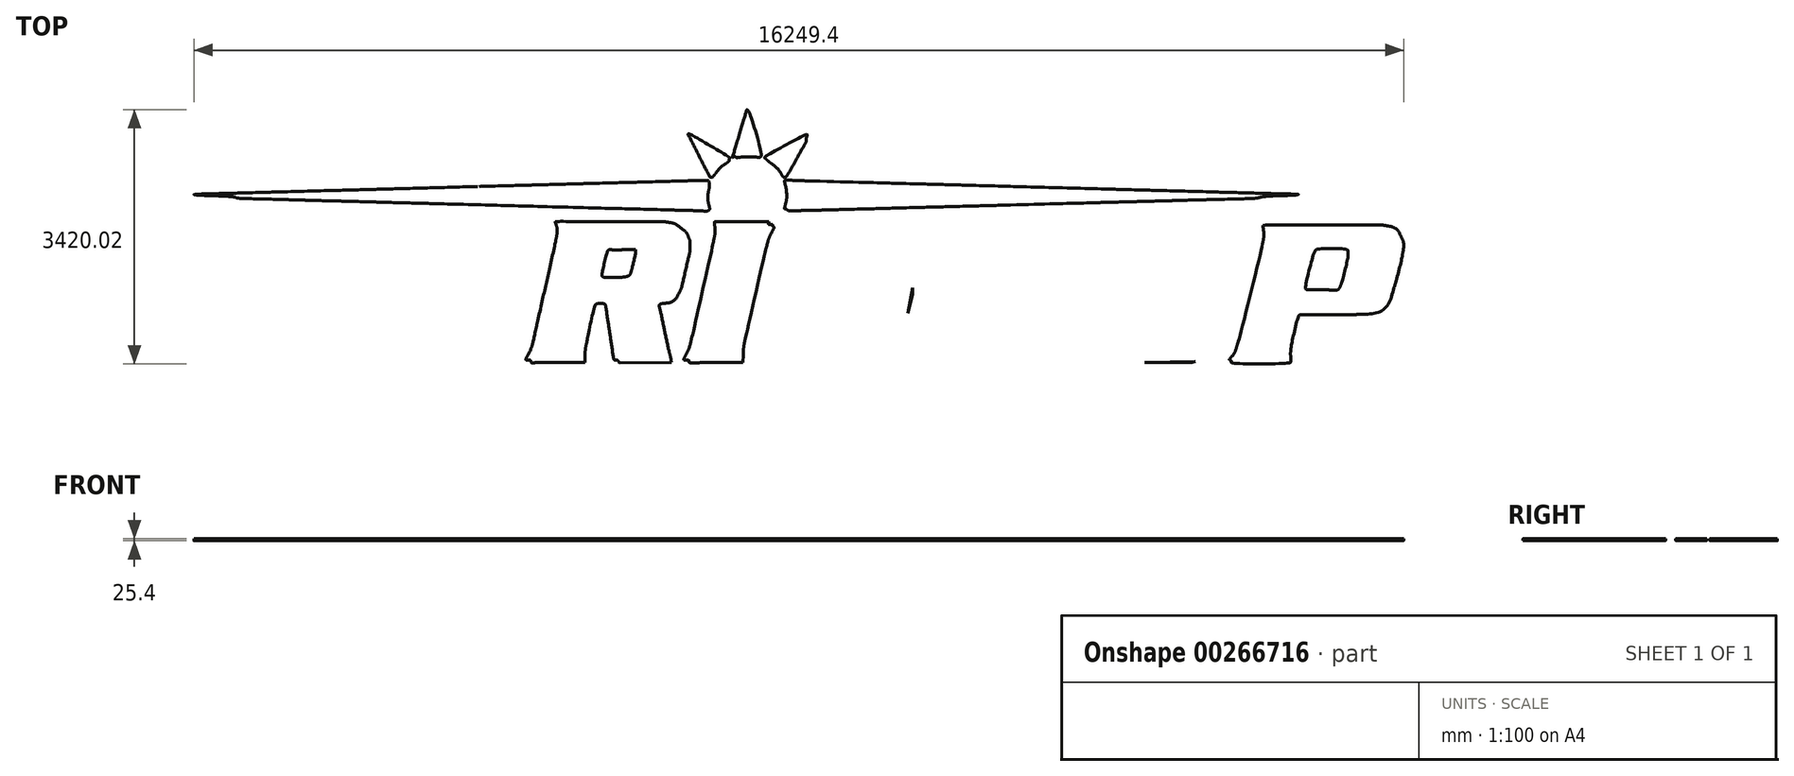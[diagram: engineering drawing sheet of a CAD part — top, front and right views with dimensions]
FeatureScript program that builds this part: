
annotation { "Feature Type Name" : "Feature", "Feature Type Description" : "" }
export const myFeature = defineFeature(function(context is Context, id is Id, definition is map)
    precondition{}
    {
        {
            var Q0;
            Q0=qCreatedBy(makeId("Top.planeOp"),FACE);
            var sketch = newSketch(context, id + "F0", { "sketchPlane" : qUnion([Q0])});
            skFitSpline(sketch, "E0", {"points": [v(-8431.98, -1796.73) * mm, v(-8427.5, -1791.33) * mm, v(-8428.15, -1778.18) * mm, v(-8434.18, -1752.53) * mm]});
            skFitSpline(sketch, "E1", {"points": [v(-8434.18, -1752.53) * mm, v(-8452.03, -1676.64) * mm, v(-8453.98, -1687.4) * mm, v(-8302.17, -1024.13) * mm]});
            skFitSpline(sketch, "E2", {"points": [v(-8302.17, -1024.13) * mm, v(-8160.3, -404.28) * mm, v(-8168.58, -438.91) * mm, v(-8162.3, -438.91) * mm]});
            skFitSpline(sketch, "E3", {"points": [v(-8162.3, -438.91) * mm, v(-8154.16, -438.91) * mm, v(-8147.34, -466.25) * mm, v(-8074.14, -792.48) * mm]});
            skFitSpline(sketch, "E4", {"points": [v(-8074.14, -792.48) * mm, v(-7911.16, -1518.8) * mm, v(-7856.82, -1758.3) * mm, v(-7853.96, -1762.94) * mm]});
            skFitSpline(sketch, "E5", {"points": [v(-7853.96, -1762.94) * mm, v(-7852.3, -1765.63) * mm, v(-7841.68, -1767.84) * mm, v(-7830.37, -1767.84) * mm]});
            skFitSpline(sketch, "E6", {"points": [v(-7830.37, -1767.84) * mm, v(-7814.48, -1767.84) * mm, v(-7806.85, -1772) * mm, v(-7796.78, -1786.13) * mm]});
            skFitSpline(sketch, "E7", {"points": [v(-6955.2, -1791.6) * mm, v(-6951.43, -1784.56) * mm, v(-6869.09, -1433.03) * mm, v(-6772.21, -1010.42) * mm]});
            skFitSpline(sketch, "E8", {"points": [v(-6772.21, -1010.42) * mm, v(-6675.33, -587.8) * mm, v(-6589.1, -216.45) * mm, v(-6580.59, -185.19) * mm]});
            skFitSpline(sketch, "E9", {"points": [v(-6580.59, -185.19) * mm, v(-6561.04, -113.45) * mm, v(-6546.58, -79.74) * mm, v(-6516.3, -35.39) * mm]});
            skFitSpline(sketch, "E10", {"points": [v(-6516.3, -35.39) * mm, v(-6490.66, 2.17) * mm, v(-6486.32, 20.8) * mm, v(-6501.8, 26.75) * mm]});
            skFitSpline(sketch, "E11", {"points": [v(-6501.8, 26.75) * mm, v(-6508.16, 29.19) * mm, v(-6510.07, 34.52) * mm, v(-6507.49, 42.64) * mm]});
            skFitSpline(sketch, "E12", {"points": [v(-6507.49, 42.64) * mm, v(-6503.95, 53.8) * mm, v(-6506.36, 54.86) * mm, v(-6535.15, 54.86) * mm]});
            skFitSpline(sketch, "E13", {"points": [v(-6535.15, 54.86) * mm, v(-6557.99, 54.86) * mm, v(-6565.84, 56.97) * mm, v(-6563.58, 62.48) * mm]});
            skFitSpline(sketch, "E14", {"points": [v(-6563.58, 62.48) * mm, v(-6550.73, 93.9) * mm, v(-6535.07, 91.44) * mm, v(-6747.62, 91.44) * mm]});
            skFitSpline(sketch, "E15", {"points": [v(-6747.62, 91.44) * mm, v(-6855.27, 91.44) * mm, v(-6943.34, 90.29) * mm, v(-6943.34, 88.88) * mm]});
            skFitSpline(sketch, "E16", {"points": [v(-6943.34, 88.88) * mm, v(-6943.34, 87.48) * mm, v(-6938.88, 68.96) * mm, v(-6933.41, 47.74) * mm]});
            skFitSpline(sketch, "E17", {"points": [v(-6933.41, 47.74) * mm, v(-6925.96, 18.76) * mm, v(-6924.4, -5.3) * mm, v(-6927.16, -48.77) * mm]});
            skFitSpline(sketch, "E18", {"points": [v(-6927.16, -48.77) * mm, v(-6930.74, -105.32) * mm, v(-6940.01, -149.28) * mm, v(-7071.16, -731.52) * mm]});
            skFitSpline(sketch, "E19", {"points": [v(-7071.16, -731.52) * mm, v(-7094.94, -837.13) * mm, v(-7131.01, -997.54) * mm, v(-7151.3, -1087.97) * mm]});
            skFitSpline(sketch, "E20", {"points": [v(-7151.3, -1087.97) * mm, v(-7187.98, -1251.36) * mm, v(-7196.45, -1280.16) * mm, v(-7204.93, -1270.15) * mm]});
            skFitSpline(sketch, "E21", {"points": [v(-7204.93, -1270.15) * mm, v(-7207.36, -1267.27) * mm, v(-7274.44, -979.63) * mm, v(-7354, -630.94) * mm]});
            skFitSpline(sketch, "E22", {"points": [v(-7354, -630.94) * mm, v(-7482.47, -67.8) * mm, v(-7500.57, 5.77) * mm, v(-7516, 27.43) * mm]});
            skFitSpline(sketch, "E23", {"points": [v(-7516, 27.43) * mm, v(-7527.17, 43.1) * mm, v(-7539.51, 52.91) * mm, v(-7550.51, 54.88) * mm]});
            skFitSpline(sketch, "E24", {"points": [v(-7550.51, 54.88) * mm, v(-7562.48, 57.02) * mm, v(-7568.72, 62.53) * mm, v(-7571.23, 73.16) * mm]});
            skLineSegment(sketch, "E25", {"start": v(-7796.78, -1786.13) * mm, "end": v(-7783.76, -1804.42) * mm});
            skLineSegment(sketch, "E26", {"start": v(-7783.76, -1804.42) * mm, "end": v(-7372.91, -1804.42) * mm});
            skLineSegment(sketch, "E27", {"start": v(-7372.91, -1804.42) * mm, "end": v(-6962.06, -1804.42) * mm});
            skLineSegment(sketch, "E28", {"start": v(-6962.06, -1804.42) * mm, "end": v(-6955.2, -1791.6) * mm});
            skFitSpline(sketch, "E29", {"points": [v(-8465.6, 74.72) * mm, v(-8463.87, 65.48) * mm, v(-8459.02, 41.14) * mm, v(-8454.83, 20.64) * mm]});
            skFitSpline(sketch, "E30", {"points": [v(-8454.83, 20.64) * mm, v(-8448.44, -10.6) * mm, v(-8448.78, -27.38) * mm, v(-8456.92, -83) * mm]});
            skFitSpline(sketch, "E31", {"points": [v(-8456.92, -83) * mm, v(-8464.25, -133.08) * mm, v(-8651.02, -975.26) * mm, v(-8769.05, -1490.47) * mm]});
            skFitSpline(sketch, "E32", {"points": [v(-8769.05, -1490.47) * mm, v(-8794.86, -1603.13) * mm, v(-8821.7, -1671.66) * mm, v(-8861.29, -1725.98) * mm]});
            skFitSpline(sketch, "E33", {"points": [v(-8861.29, -1725.98) * mm, v(-8872.6, -1741.52) * mm, v(-8881.87, -1757.3) * mm, v(-8881.87, -1761.03) * mm]});
            skFitSpline(sketch, "E34", {"points": [v(-8881.87, -1761.03) * mm, v(-8881.87, -1765.14) * mm, v(-8869.7, -1767.84) * mm, v(-8851.2, -1767.84) * mm]});
            skFitSpline(sketch, "E35", {"points": [v(-8851.2, -1767.84) * mm, v(-8829.27, -1767.84) * mm, v(-8819.72, -1770.44) * mm, v(-8817.67, -1776.98) * mm]});
            skFitSpline(sketch, "E36", {"points": [v(-8817.67, -1776.98) * mm, v(-8816.1, -1782.01) * mm, v(-8813.53, -1790.24) * mm, v(-8811.96, -1795.27) * mm]});
            skFitSpline(sketch, "E37", {"points": [v(-8811.96, -1795.27) * mm, v(-8809.5, -1803.14) * mm, v(-8783.17, -1804.41) * mm, v(-8623.73, -1804.41) * mm]});
            skFitSpline(sketch, "E38", {"points": [v(-8623.73, -1804.41) * mm, v(-8482, -1804.41) * mm, v(-8436.85, -1802.6) * mm, v(-8431.98, -1796.73) * mm]});
            skLineSegment(sketch, "E39", {"start": v(-7571.23, 73.16) * mm, "end": v(-7574.83, 88.4) * mm});
            skLineSegment(sketch, "E40", {"start": v(-7574.83, 88.4) * mm, "end": v(-8021.78, 89.96) * mm});
            skLineSegment(sketch, "E41", {"start": v(-8021.78, 89.96) * mm, "end": v(-8468.74, 91.52) * mm});
            skLineSegment(sketch, "E42", {"start": v(-8468.74, 91.52) * mm, "end": v(-8465.6, 74.72) * mm});
            skLineSegment(sketch, "E43", {"start": v(-8431.98, -1796.73) * mm, "end": v(-8431.98, -1796.73) * mm});
            skFitSpline(sketch, "E44", {"points": [v(-5178.94, -1795.17) * mm, v(-4971.29, -1758.95) * mm, v(-4859.54, -1649.36) * mm, v(-4776.79, -1400.78) * mm]});
            skFitSpline(sketch, "E45", {"points": [v(-4776.79, -1400.78) * mm, v(-4759.4, -1348.54) * mm, v(-4707.32, -1133.65) * mm, v(-4630.12, -795.52) * mm]});
            skFitSpline(sketch, "E46", {"points": [v(-4630.12, -795.52) * mm, v(-4564.28, -507.18) * mm, v(-4502.2, -240.06) * mm, v(-4492.15, -201.92) * mm]});
            skFitSpline(sketch, "E47", {"points": [v(-4492.15, -201.92) * mm, v(-4471.17, -122.26) * mm, v(-4447.43, -66.45) * mm, v(-4416.71, -24.6) * mm]});
            skFitSpline(sketch, "E48", {"points": [v(-4416.71, -24.6) * mm, v(-4392.05, 9) * mm, v(-4390.74, 15.47) * mm, v(-4406.86, 24.1) * mm]});
            skFitSpline(sketch, "E49", {"points": [v(-4406.86, 24.1) * mm, v(-4414.56, 28.21) * mm, v(-4417.41, 34.48) * mm, v(-4415.3, 42.6) * mm]});
            skFitSpline(sketch, "E50", {"points": [v(-4415.3, 42.6) * mm, v(-4412.42, 53.57) * mm, v(-4415.02, 54.87) * mm, v(-4439.87, 54.87) * mm]});
            skFitSpline(sketch, "E51", {"points": [v(-4439.87, 54.87) * mm, v(-4466.92, 54.87) * mm, v(-4480.96, 62.32) * mm, v(-4468.47, 70.05) * mm]});
            skFitSpline(sketch, "E52", {"points": [v(-4468.47, 70.05) * mm, v(-4465.06, 72.15) * mm, v(-4462.27, 77.83) * mm, v(-4462.27, 82.66) * mm]});
            skFitSpline(sketch, "E53", {"points": [v(-4462.27, 82.66) * mm, v(-4462.27, 90.12) * mm, v(-4491.12, 91.44) * mm, v(-4653.94, 91.44) * mm]});
            skFitSpline(sketch, "E54", {"points": [v(-4653.94, 91.44) * mm, v(-4759.35, 91.44) * mm, v(-4846.99, 89.2) * mm, v(-4848.68, 86.46) * mm]});
            skFitSpline(sketch, "E55", {"points": [v(-4848.68, 86.46) * mm, v(-4850.37, 83.72) * mm, v(-4847.5, 69.32) * mm, v(-4842.29, 54.46) * mm]});
            skFitSpline(sketch, "E56", {"points": [v(-4842.29, 54.46) * mm, v(-4829.89, 19.09) * mm, v(-4830.12, -50.34) * mm, v(-4842.88, -118.87) * mm]});
            skFitSpline(sketch, "E57", {"points": [v(-4842.88, -118.87) * mm, v(-4848.5, -149.04) * mm, v(-4892.91, -350.67) * mm, v(-4941.58, -566.92) * mm]});
            skFitSpline(sketch, "E58", {"points": [v(-4941.58, -566.92) * mm, v(-4990.24, -783.18) * mm, v(-5045.1, -1027.32) * mm, v(-5063.48, -1109.47) * mm]});
            skFitSpline(sketch, "E59", {"points": [v(-5063.48, -1109.47) * mm, v(-5123.47, -1377.56) * mm, v(-5133.99, -1408.78) * mm, v(-5172.31, -1432.47) * mm]});
            skFitSpline(sketch, "E60", {"points": [v(-5172.31, -1432.47) * mm, v(-5216.4, -1459.71) * mm, v(-5256.63, -1462.82) * mm, v(-5567.47, -1462.93) * mm]});
            skFitSpline(sketch, "E61", {"points": [v(-5567.47, -1462.93) * mm, v(-5896.03, -1463.05) * mm, v(-5889.2, -1463.92) * mm, v(-5900.87, -1420.56) * mm]});
            skFitSpline(sketch, "E62", {"points": [v(-5900.87, -1420.56) * mm, v(-5905.23, -1404.4) * mm, v(-5905.46, -1384.81) * mm, v(-5901.59, -1361.16) * mm]});
            skFitSpline(sketch, "E63", {"points": [v(-5901.59, -1361.16) * mm, v(-5896.4, -1329.49) * mm, v(-5669.8, -336.13) * mm, v(-5647.4, -246.88) * mm]});
            skFitSpline(sketch, "E64", {"points": [v(-5647.4, -246.88) * mm, v(-5629.38, -175.1) * mm, v(-5613, -130.05) * mm, v(-5579.02, -58.85) * mm]});
            skFitSpline(sketch, "E65", {"points": [v(-5579.02, -58.85) * mm, v(-5547.23, 7.76) * mm, v(-5545.37, 13.96) * mm, v(-5555.1, 21.07) * mm]});
            skFitSpline(sketch, "E66", {"points": [v(-5555.1, 21.07) * mm, v(-5560.9, 25.31) * mm, v(-5565.65, 34.65) * mm, v(-5565.65, 41.82) * mm]});
            skFitSpline(sketch, "E67", {"points": [v(-5565.65, 41.82) * mm, v(-5565.65, 53.25) * mm, v(-5569.1, 54.87) * mm, v(-5593.56, 54.87) * mm]});
            skFitSpline(sketch, "E68", {"points": [v(-5593.56, 54.87) * mm, v(-5621.41, 54.87) * mm, v(-5621.47, 54.9) * mm, v(-5617.46, 73.16) * mm]});
            skFitSpline(sketch, "E69", {"points": [v(-6342.31, 22.86) * mm, v(-6339.73, -25.35) * mm, v(-6341.45, -64.09) * mm, v(-6348.13, -107.57) * mm]});
            skFitSpline(sketch, "E70", {"points": [v(-6348.13, -107.57) * mm, v(-6353.35, -141.6) * mm, v(-6410.07, -402.2) * mm, v(-6474.17, -686.7) * mm]});
            skFitSpline(sketch, "E71", {"points": [v(-6474.17, -686.7) * mm, v(-6538.27, -971.19) * mm, v(-6595.73, -1232.76) * mm, v(-6601.85, -1267.96) * mm]});
            skFitSpline(sketch, "E72", {"points": [v(-6601.85, -1267.96) * mm, v(-6632.1, -1441.75) * mm, v(-6620.03, -1560) * mm, v(-6563.46, -1644.14) * mm]});
            skFitSpline(sketch, "E73", {"points": [v(-6563.46, -1644.14) * mm, v(-6522.9, -1704.48) * mm, v(-6406.1, -1776.16) * mm, v(-6318.5, -1794.5) * mm]});
            skFitSpline(sketch, "E74", {"points": [v(-6318.5, -1794.5) * mm, v(-6253.74, -1808.04) * mm, v(-5256.15, -1808.63) * mm, v(-5178.94, -1795.16) * mm]});
            skLineSegment(sketch, "E75", {"start": v(-5617.46, 73.16) * mm, "end": v(-5613.45, 91.44) * mm});
            skLineSegment(sketch, "E76", {"start": v(-5613.45, 91.44) * mm, "end": v(-5979.72, 91.44) * mm});
            skLineSegment(sketch, "E77", {"start": v(-5979.72, 91.44) * mm, "end": v(-6345.99, 91.44) * mm});
            skLineSegment(sketch, "E78", {"start": v(-6345.99, 91.44) * mm, "end": v(-6342.31, 22.86) * mm});
            skLineSegment(sketch, "E79", {"start": v(-5178.94, -1795.16) * mm, "end": v(-5178.94, -1795.17) * mm});
            skLineSegment(sketch, "E80", {"start": v(-5178.94, -1795.17) * mm, "end": v(-5178.94, -1795.16) * mm});
            skFitSpline(sketch, "E81", {"points": [v(-3486.19, -1697.73) * mm, v(-3484.1, -1640.73) * mm, v(-3479.05, -1579.01) * mm, v(-3474.93, -1560.57) * mm]});
            skFitSpline(sketch, "E82", {"points": [v(-3474.93, -1560.57) * mm, v(-3391.53, -1186.6) * mm, v(-3185.68, -299.95) * mm, v(-3180.94, -294.24) * mm]});
            skFitSpline(sketch, "E83", {"points": [v(-3180.94, -294.24) * mm, v(-3176.03, -288.32) * mm, v(-3133.43, -286.5) * mm, v(-2999.77, -286.5) * mm]});
            skFitSpline(sketch, "E84", {"points": [v(-2999.77, -286.5) * mm, v(-2806.66, -286.5) * mm, v(-2776.98, -290.46) * mm, v(-2723.57, -323.33) * mm]});
            skFitSpline(sketch, "E85", {"points": [v(-2723.57, -323.33) * mm, v(-2689.82, -344.1) * mm, v(-2678.79, -345.64) * mm, v(-2671.04, -330.7) * mm]});
            skFitSpline(sketch, "E86", {"points": [v(-2671.04, -330.7) * mm, v(-2668, -324.84) * mm, v(-2659.1, -246.5) * mm, v(-2651.27, -156.62) * mm]});
            skFitSpline(sketch, "E87", {"points": [v(-2651.27, -156.62) * mm, v(-2639.99, -27.31) * mm, v(-2638.56, 8.94) * mm, v(-2644.4, 17.11) * mm]});
            skFitSpline(sketch, "E88", {"points": [v(-2644.4, 17.11) * mm, v(-2648.47, 22.8) * mm, v(-2654.46, 33.6) * mm, v(-2657.72, 41.15) * mm]});
            skFitSpline(sketch, "E89", {"points": [v(-2657.72, 41.15) * mm, v(-2662.23, 51.59) * mm, v(-2668.7, 54.87) * mm, v(-2684.73, 54.87) * mm]});
            skFitSpline(sketch, "E90", {"points": [v(-2684.73, 54.87) * mm, v(-2703.2, 54.87) * mm, v(-2706.05, 56.95) * mm, v(-2707.74, 71.63) * mm]});
            skFitSpline(sketch, "E91", {"points": [v(-4308.91, 74.7) * mm, v(-4332.45, 15.16) * mm, v(-4431.8, -265.13) * mm, v(-4431.8, -272) * mm]});
            skFitSpline(sketch, "E92", {"points": [v(-4320.6, -328.43) * mm, v(-4251.94, -293.4) * mm, v(-4237.02, -290.88) * mm, v(-4076.17, -287.06) * mm]});
            skFitSpline(sketch, "E93", {"points": [v(-4076.17, -287.06) * mm, v(-3915.05, -283.23) * mm, v(-3909.97, -284.02) * mm, v(-3916.42, -311.83) * mm]});
            skFitSpline(sketch, "E94", {"points": [v(-3916.42, -311.83) * mm, v(-3918.25, -319.7) * mm, v(-3961.02, -509.93) * mm, v(-4011.47, -734.56) * mm]});
            skFitSpline(sketch, "E95", {"points": [v(-4011.47, -734.56) * mm, v(-4208.78, -1613.19) * mm, v(-4203.84, -1593.75) * mm, v(-4256.13, -1696.03) * mm]});
            skFitSpline(sketch, "E96", {"points": [v(-4256.13, -1696.03) * mm, v(-4272.8, -1728.62) * mm, v(-4284.69, -1758.1) * mm, v(-4282.55, -1761.56) * mm]});
            skFitSpline(sketch, "E97", {"points": [v(-4282.55, -1761.56) * mm, v(-4280.42, -1765.01) * mm, v(-4266.4, -1767.84) * mm, v(-4251.4, -1767.84) * mm]});
            skFitSpline(sketch, "E98", {"points": [v(-4251.4, -1767.84) * mm, v(-4232.5, -1767.84) * mm, v(-4223.27, -1770.64) * mm, v(-4221.29, -1776.98) * mm]});
            skFitSpline(sketch, "E99", {"points": [v(-4221.29, -1776.98) * mm, v(-4219.72, -1782) * mm, v(-4217.14, -1790.26) * mm, v(-4215.56, -1795.32) * mm]});
            skFitSpline(sketch, "E100", {"points": [v(-4215.56, -1795.32) * mm, v(-4213.03, -1803.4) * mm, v(-4168.96, -1804.32) * mm, v(-3851.32, -1802.94) * mm]});
            skLineSegment(sketch, "E101", {"start": v(-2707.74, 71.63) * mm, "end": v(-2709.67, 88.4) * mm});
            skLineSegment(sketch, "E102", {"start": v(-2709.67, 88.4) * mm, "end": v(-3505.97, 89.94) * mm});
            skLineSegment(sketch, "E103", {"start": v(-3505.97, 89.94) * mm, "end": v(-4302.28, 91.49) * mm});
            skLineSegment(sketch, "E104", {"start": v(-4302.28, 91.49) * mm, "end": v(-4308.91, 74.7) * mm});
            skLineSegment(sketch, "E105", {"start": v(-3851.32, -1802.94) * mm, "end": v(-3489.96, -1801.36) * mm});
            skLineSegment(sketch, "E106", {"start": v(-3489.96, -1801.36) * mm, "end": v(-3486.19, -1697.73) * mm});
            skLineSegment(sketch, "E107", {"start": v(-3486.19, -1697.73) * mm, "end": v(-3486.19, -1697.73) * mm});
            skFitSpline(sketch, "E108", {"points": [v(-2117.44, -1718.33) * mm, v(-2116.83, -1662.92) * mm, v(-2112.29, -1613.23) * mm, v(-2103.8, -1568.98) * mm]});
            skFitSpline(sketch, "E109", {"points": [v(-2103.8, -1568.98) * mm, v(-2080.04, -1445) * mm, v(-1982.48, -1029.06) * mm, v(-1975.53, -1022.1) * mm]});
            skFitSpline(sketch, "E110", {"points": [v(-1975.53, -1022.1) * mm, v(-1967.77, -1014.35) * mm, v(-1885.52, -1008.61) * mm, v(-1863.02, -1014.26) * mm]});
            skFitSpline(sketch, "E111", {"points": [v(-1863.02, -1014.26) * mm, v(-1855, -1016.27) * mm, v(-1847.11, -1021.37) * mm, v(-1845.5, -1025.6) * mm]});
            skFitSpline(sketch, "E112", {"points": [v(-1845.5, -1025.6) * mm, v(-1843.89, -1029.81) * mm, v(-1818.73, -1192.37) * mm, v(-1789.6, -1386.84) * mm]});
            skFitSpline(sketch, "E113", {"points": [v(-1789.6, -1386.84) * mm, v(-1760.45, -1581.3) * mm, v(-1734.1, -1746.58) * mm, v(-1731.02, -1754.12) * mm]});
            skFitSpline(sketch, "E114", {"points": [v(-1731.02, -1754.12) * mm, v(-1726.74, -1764.62) * mm, v(-1720.49, -1767.84) * mm, v(-1704.38, -1767.84) * mm]});
            skFitSpline(sketch, "E115", {"points": [v(-1704.38, -1767.84) * mm, v(-1687.93, -1767.84) * mm, v(-1680.47, -1771.85) * mm, v(-1670.27, -1786.17) * mm]});
            skFitSpline(sketch, "E116", {"points": [v(-961.22, -1780.03) * mm, v(-961.82, -1768.3) * mm, v(-970.52, -1727.15) * mm, v(-980.55, -1688.59) * mm]});
            skFitSpline(sketch, "E117", {"points": [v(-980.55, -1688.59) * mm, v(-990.57, -1650.03) * mm, v(-1026.83, -1485.94) * mm, v(-1061.12, -1323.95) * mm]});
            skFitSpline(sketch, "E118", {"points": [v(-1061.12, -1323.95) * mm, v(-1114.17, -1073.28) * mm, v(-1122.2, -1028.23) * mm, v(-1114.94, -1021.5) * mm]});
            skFitSpline(sketch, "E119", {"points": [v(-1114.94, -1021.5) * mm, v(-1110.26, -1017.15) * mm, v(-1085.85, -1010.44) * mm, v(-1060.7, -1006.58) * mm]});
            skFitSpline(sketch, "E120", {"points": [v(-1060.7, -1006.58) * mm, v(-970.11, -992.67) * mm, v(-899.87, -944.3) * mm, v(-857.68, -866.74) * mm]});
            skFitSpline(sketch, "E121", {"points": [v(-857.68, -866.74) * mm, v(-829.64, -815.22) * mm, v(-813.72, -759.89) * mm, v(-761.15, -531.43) * mm]});
            skFitSpline(sketch, "E122", {"points": [v(-761.15, -531.43) * mm, v(-712.97, -322.01) * mm, v(-711.1, -311.11) * mm, v(-710.93, -237.74) * mm]});
            skFitSpline(sketch, "E123", {"points": [v(-710.93, -237.74) * mm, v(-710.79, -174.01) * mm, v(-712.86, -156.27) * mm, v(-723.67, -129.35) * mm]});
            skFitSpline(sketch, "E124", {"points": [v(-723.67, -129.35) * mm, v(-743.02, -81.13) * mm, v(-772.85, -38.1) * mm, v(-802, -16.36) * mm]});
            skFitSpline(sketch, "E125", {"points": [v(-802, -16.36) * mm, v(-901.62, 57.95) * mm, v(-922.42, 68.11) * mm, v(-1003.91, 82.32) * mm]});
            skFitSpline(sketch, "E126", {"points": [v(-1003.91, 82.32) * mm, v(-1048.37, 90.08) * mm, v(-1165.66, 91.44) * mm, v(-1786.93, 91.44) * mm]});
            skFitSpline(sketch, "E127", {"points": [v(-1786.93, 91.44) * mm, v(-2188.82, 91.44) * mm, v(-2517.62, 89.39) * mm, v(-2517.58, 86.87) * mm]});
            skFitSpline(sketch, "E128", {"points": [v(-2517.58, 86.87) * mm, v(-2517.52, 84.36) * mm, v(-2513.43, 68.83) * mm, v(-2508.44, 52.38) * mm]});
            skFitSpline(sketch, "E129", {"points": [v(-2508.44, 52.38) * mm, v(-2495.9, 11.04) * mm, v(-2497, -76.54) * mm, v(-2511.03, -152.89) * mm]});
            skFitSpline(sketch, "E130", {"points": [v(-2511.03, -152.89) * mm, v(-2517.45, -187.82) * mm, v(-2576.58, -455.06) * mm, v(-2642.43, -746.76) * mm]});
            skFitSpline(sketch, "E131", {"points": [v(-2642.43, -746.76) * mm, v(-2708.29, -1038.45) * mm, v(-2770.42, -1314.14) * mm, v(-2780.5, -1359.4) * mm]});
            skFitSpline(sketch, "E132", {"points": [v(-2780.5, -1359.4) * mm, v(-2823.22, -1551.2) * mm, v(-2842.2, -1612.65) * mm, v(-2884.19, -1695.1) * mm]});
            skFitSpline(sketch, "E133", {"points": [v(-2884.19, -1695.1) * mm, v(-2900.52, -1727.2) * mm, v(-2913.89, -1756.68) * mm, v(-2913.89, -1760.64) * mm]});
            skFitSpline(sketch, "E134", {"points": [v(-2913.89, -1760.64) * mm, v(-2913.89, -1765.22) * mm, v(-2902.73, -1767.84) * mm, v(-2883.22, -1767.84) * mm]});
            skFitSpline(sketch, "E135", {"points": [v(-2883.22, -1767.84) * mm, v(-2861.29, -1767.84) * mm, v(-2851.73, -1770.44) * mm, v(-2849.69, -1776.98) * mm]});
            skFitSpline(sketch, "E136", {"points": [v(-2849.69, -1776.98) * mm, v(-2848.12, -1782) * mm, v(-2845.54, -1790.26) * mm, v(-2843.96, -1795.32) * mm]});
            skFitSpline(sketch, "E137", {"points": [v(-2843.96, -1795.32) * mm, v(-2841.43, -1803.4) * mm, v(-2797.36, -1804.32) * mm, v(-2479.72, -1802.94) * mm]});
            skLineSegment(sketch, "E138", {"start": v(-1670.27, -1786.17) * mm, "end": v(-1657.21, -1804.51) * mm});
            skLineSegment(sketch, "E139", {"start": v(-1657.21, -1804.51) * mm, "end": v(-1308.67, -1802.94) * mm});
            skLineSegment(sketch, "E140", {"start": v(-1308.67, -1802.94) * mm, "end": v(-960.12, -1801.37) * mm});
            skLineSegment(sketch, "E141", {"start": v(-960.12, -1801.37) * mm, "end": v(-961.22, -1780.03) * mm});
            skLineSegment(sketch, "E142", {"start": v(-2479.72, -1802.94) * mm, "end": v(-2118.36, -1801.36) * mm});
            skLineSegment(sketch, "E143", {"start": v(-2118.36, -1801.36) * mm, "end": v(-2117.44, -1718.33) * mm});
            skLineSegment(sketch, "E144", {"start": v(-2117.44, -1718.33) * mm, "end": v(-2117.44, -1718.33) * mm});
            skFitSpline(sketch, "E145", {"points": [v(-1882.14, -648.23) * mm, v(-1886.33, -646.54) * mm, v(-1889.76, -640.1) * mm, v(-1889.76, -633.94) * mm]});
            skFitSpline(sketch, "E146", {"points": [v(-1889.76, -633.94) * mm, v(-1889.76, -614.02) * mm, v(-1815.9, -302.15) * mm, v(-1809.3, -294.2) * mm]});
            skFitSpline(sketch, "E147", {"points": [v(-1809.3, -294.2) * mm, v(-1804.43, -288.32) * mm, v(-1760, -286.5) * mm, v(-1620.79, -286.5) * mm]});
            skFitSpline(sketch, "E148", {"points": [v(-1438.66, -300.88) * mm, v(-1438.66, -317.99) * mm, v(-1482.61, -518.17) * mm, v(-1497.54, -569.02) * mm]});
            skFitSpline(sketch, "E149", {"points": [v(-1497.54, -569.02) * mm, v(-1510.1, -611.82) * mm, v(-1531.55, -636.52) * mm, v(-1563.98, -645.53) * mm]});
            skFitSpline(sketch, "E150", {"points": [v(-1563.98, -645.53) * mm, v(-1587.8, -652.14) * mm, v(-1866.58, -654.5) * mm, v(-1882.14, -648.23) * mm]});
            skLineSegment(sketch, "E151", {"start": v(-1620.79, -286.5) * mm, "end": v(-1438.66, -286.5) * mm});
            skLineSegment(sketch, "E152", {"start": v(-1438.66, -286.5) * mm, "end": v(-1438.66, -300.88) * mm});
            skFitSpline(sketch, "E153", {"points": [v(6.87, -1697.74) * mm, v(9.4, -1628.78) * mm, v(14.9, -1574.73) * mm, v(23.27, -1536.2) * mm]});
            skFitSpline(sketch, "E154", {"points": [v(23.27, -1536.2) * mm, v(46.64, -1428.6) * mm, v(305.4, -302.24) * mm, v(320.44, -242.55) * mm]});
            skFitSpline(sketch, "E155", {"points": [v(320.44, -242.55) * mm, v(341.1, -160.68) * mm, v(362.15, -103.78) * mm, v(395.2, -40.56) * mm]});
            skFitSpline(sketch, "E156", {"points": [v(395.2, -40.56) * mm, v(422.75, 12.12) * mm, v(423.13, 13.57) * mm, v(411.35, 22.2) * mm]});
            skFitSpline(sketch, "E157", {"points": [v(411.35, 22.2) * mm, v(404.71, 27.06) * mm, v(399.29, 35.72) * mm, v(399.29, 41.43) * mm]});
            skFitSpline(sketch, "E158", {"points": [v(399.29, 41.43) * mm, v(399.29, 49.33) * mm, v(392.93, 52.27) * mm, v(372.7, 53.72) * mm]});
            skFitSpline(sketch, "E159", {"points": [v(372.7, 53.72) * mm, v(346.82, 55.58) * mm, v(346.2, 56.11) * mm, v(349.68, 73.53) * mm]});
            skFitSpline(sketch, "E160", {"points": [v(-11.98, 91.44) * mm, v(-212.87, 91.44) * mm, v(-378.42, 89.38) * mm, v(-379.87, 86.86) * mm]});
            skFitSpline(sketch, "E161", {"points": [v(-379.87, 86.86) * mm, v(-381.32, 84.35) * mm, v(-379.79, 61.76) * mm, v(-376.48, 36.67) * mm]});
            skFitSpline(sketch, "E162", {"points": [v(-376.48, 36.67) * mm, v(-369.97, -12.63) * mm, v(-376.28, -90.57) * mm, v(-393.67, -175.57) * mm]});
            skFitSpline(sketch, "E163", {"points": [v(-393.67, -175.57) * mm, v(-406.14, -236.53) * mm, v(-680.38, -1454.73) * mm, v(-692.43, -1502.67) * mm]});
            skFitSpline(sketch, "E164", {"points": [v(-692.43, -1502.67) * mm, v(-710.55, -1574.8) * mm, v(-733.56, -1637.74) * mm, v(-762.78, -1695.12) * mm]});
            skFitSpline(sketch, "E165", {"points": [v(-762.78, -1695.12) * mm, v(-779.11, -1727.2) * mm, v(-792.48, -1756.69) * mm, v(-792.48, -1760.65) * mm]});
            skFitSpline(sketch, "E166", {"points": [v(-792.48, -1760.65) * mm, v(-792.48, -1764.95) * mm, v(-782.89, -1767.84) * mm, v(-768.6, -1767.84) * mm]});
            skFitSpline(sketch, "E167", {"points": [v(-768.6, -1767.84) * mm, v(-737.43, -1767.84) * mm, v(-725.42, -1772.83) * mm, v(-725.42, -1785.77) * mm]});
            skFitSpline(sketch, "E168", {"points": [v(-725.42, -1785.77) * mm, v(-725.42, -1791.56) * mm, v(-723.57, -1798.14) * mm, v(-721.31, -1800.4) * mm]});
            skFitSpline(sketch, "E169", {"points": [v(-721.31, -1800.4) * mm, v(-719.05, -1802.67) * mm, v(-555.14, -1803.8) * mm, v(-357.08, -1802.94) * mm]});
            skLineSegment(sketch, "E170", {"start": v(349.68, 73.53) * mm, "end": v(353.26, 91.44) * mm});
            skLineSegment(sketch, "E171", {"start": v(353.26, 91.44) * mm, "end": v(-11.98, 91.44) * mm});
            skLineSegment(sketch, "E172", {"start": v(-357.08, -1802.94) * mm, "end": v(3.05, -1801.37) * mm});
            skLineSegment(sketch, "E173", {"start": v(3.05, -1801.37) * mm, "end": v(6.87, -1697.74) * mm});
            skLineSegment(sketch, "E174", {"start": v(6.87, -1697.74) * mm, "end": v(6.87, -1697.74) * mm});
            skFitSpline(sketch, "E175", {"points": [v(1794.1, -1787.18) * mm, v(1966.56, -1737.53) * mm, v(2066.19, -1638) * mm, v(2132.99, -1448.6) * mm]});
            skFitSpline(sketch, "E176", {"points": [v(2132.99, -1448.6) * mm, v(2143.48, -1418.86) * mm, v(2181.35, -1278.96) * mm, v(2217.16, -1137.7) * mm]});
            skLineSegment(sketch, "E177", {"start": v(38.18, 40.95) * mm, "end": v(38.18, 40.95) * mm});
            skFitSpline(sketch, "E178", {"points": [v(2282.6, -798.47) * mm, v(2282.95, -717.59) * mm, v(2282.6, -715.33) * mm, v(2263.23, -676) * mm]});
            skFitSpline(sketch, "E179", {"points": [v(2263.23, -676) * mm, v(2224.65, -597.57) * mm, v(2178.05, -560.39) * mm, v(2086.81, -535.22) * mm]});
            skFitSpline(sketch, "E180", {"points": [v(2086.81, -535.22) * mm, v(2041.24, -522.65) * mm, v(2023.2, -521.91) * mm, v(1682.22, -518.6) * mm]});
            skFitSpline(sketch, "E181", {"points": [v(1682.22, -518.6) * mm, v(1354.32, -515.4) * mm, v(1323.98, -514.24) * mm, v(1308.84, -504.3) * mm]});
            skFitSpline(sketch, "E182", {"points": [v(1308.84, -504.3) * mm, v(1299.77, -498.36) * mm, v(1292.35, -492.12) * mm, v(1292.35, -490.43) * mm]});
            skFitSpline(sketch, "E183", {"points": [v(1292.35, -490.43) * mm, v(1292.35, -488.75) * mm, v(1301, -452.87) * mm, v(1311.55, -410.71) * mm]});
            skFitSpline(sketch, "E184", {"points": [v(1311.55, -410.71) * mm, v(1332.97, -325.2) * mm, v(1346.42, -302.9) * mm, v(1382.66, -292.83) * mm]});
            skFitSpline(sketch, "E185", {"points": [v(1382.66, -292.83) * mm, v(1396.96, -288.86) * mm, v(1551.5, -286.61) * mm, v(1807.47, -286.66) * mm]});
            skFitSpline(sketch, "E186", {"points": [v(1807.47, -286.66) * mm, v(2243.8, -286.74) * mm, v(2249.78, -287.12) * mm, v(2336.22, -321.04) * mm]});
            skFitSpline(sketch, "E187", {"points": [v(2336.22, -321.04) * mm, v(2374.14, -335.92) * mm, v(2378.8, -336.53) * mm, v(2387.51, -327.83) * mm]});
            skFitSpline(sketch, "E188", {"points": [v(2387.51, -327.83) * mm, v(2394.95, -320.39) * mm, v(2400.06, -282.68) * mm, v(2410.33, -159.32) * mm]});
            skFitSpline(sketch, "E189", {"points": [v(2410.33, -159.32) * mm, v(2417.81, -69.53) * mm, v(2421.39, 4.34) * mm, v(2418.55, 10.47) * mm]});
            skFitSpline(sketch, "E190", {"points": [v(2418.55, 10.47) * mm, v(2415.8, 16.44) * mm, v(2409.88, 27.67) * mm, v(2405.4, 35.43) * mm]});
            skLineSegment(sketch, "E191", {"start": v(2217.16, -1137.7) * mm, "end": v(2282.26, -880.88) * mm});
            skLineSegment(sketch, "E192", {"start": v(2282.26, -880.88) * mm, "end": v(2282.6, -798.47) * mm});
            skLineSegment(sketch, "E193", {"start": v(2282.6, -798.47) * mm, "end": v(2217.16, -1137.7) * mm});
            skFitSpline(sketch, "E194", {"points": [v(1756.15, 48.96) * mm, v(1393.39, 48.64) * mm, v(1095.29, 45.9) * mm, v(1069.57, 42.63) * mm]});
            skFitSpline(sketch, "E195", {"points": [v(1069.57, 42.63) * mm, v(1019.2, 36.24) * mm, v(948.75, 14.36) * mm, v(900.34, -9.95) * mm]});
            skFitSpline(sketch, "E196", {"points": [v(900.34, -9.95) * mm, v(799.55, -60.56) * mm, v(699.85, -163.5) * mm, v(657.44, -260.75) * mm]});
            skFitSpline(sketch, "E197", {"points": [v(657.44, -260.75) * mm, v(632.14, -318.78) * mm, v(619.84, -361.45) * mm, v(557.78, -606.56) * mm]});
            skFitSpline(sketch, "E198", {"points": [v(557.78, -606.56) * mm, v(488.47, -880.3) * mm, v(475.32, -957.46) * mm, v(487.1, -1021.09) * mm]});
            skFitSpline(sketch, "E199", {"points": [v(487.1, -1021.09) * mm, v(500.15, -1091.47) * mm, v(538.55, -1150.27) * mm, v(589.6, -1178.06) * mm]});
            skFitSpline(sketch, "E200", {"points": [v(589.6, -1178.06) * mm, v(657.8, -1215.18) * mm, v(656.5, -1215.07) * mm, v(1076.54, -1218.82) * mm]});
            skFitSpline(sketch, "E201", {"points": [v(1076.54, -1218.82) * mm, v(1499.7, -1222.6) * mm, v(1485.87, -1221.23) * mm, v(1479.2, -1258.55) * mm]});
            skFitSpline(sketch, "E202", {"points": [v(1479.2, -1258.55) * mm, v(1477.39, -1268.76) * mm, v(1467.5, -1314.15) * mm, v(1457.23, -1359.41) * mm]});
            skFitSpline(sketch, "E203", {"points": [v(1457.23, -1359.41) * mm, v(1440.87, -1431.55) * mm, v(1436.26, -1443.81) * mm, v(1419.93, -1458.74) * mm]});
            skLineSegment(sketch, "E204", {"start": v(2405.4, 35.43) * mm, "end": v(2397.28, 49.52) * mm});
            skLineSegment(sketch, "E205", {"start": v(2397.28, 49.52) * mm, "end": v(1756.15, 48.96) * mm});
            skFitSpline(sketch, "E206", {"points": [v(467.36, -1448.96) * mm, v(398.23, -1424.64) * mm, v(370.66, -1423.23) * mm, v(362.81, -1443.6) * mm]});
            skFitSpline(sketch, "E207", {"points": [v(362.81, -1443.6) * mm, v(360.63, -1449.27) * mm, v(354.98, -1499.16) * mm, v(350.26, -1554.48) * mm]});
            skFitSpline(sketch, "E208", {"points": [v(350.26, -1554.48) * mm, v(345.53, -1609.8) * mm, v(338.62, -1677.38) * mm, v(334.9, -1704.65) * mm]});
            skFitSpline(sketch, "E209", {"points": [v(334.9, -1704.65) * mm, v(328.27, -1753.15) * mm, v(328.47, -1754.77) * mm, v(344.08, -1779.5) * mm]});
            skLineSegment(sketch, "E210", {"start": v(1419.93, -1458.74) * mm, "end": v(1401.3, -1475.77) * mm});
            skLineSegment(sketch, "E211", {"start": v(467.36, -1448.96) * mm, "end": v(1419.93, -1458.74) * mm});
            skFitSpline(sketch, "E212", {"points": [v(2978.48, -1719.08) * mm, v(2978.83, -1669.12) * mm, v(2983.08, -1616.42) * mm, v(2989.29, -1584.96) * mm]});
            skFitSpline(sketch, "E213", {"points": [v(2989.29, -1584.96) * mm, v(3007.69, -1491.69) * mm, v(3125.69, -1029.35) * mm, v(3132.95, -1022.08) * mm]});
            skFitSpline(sketch, "E214", {"points": [v(3132.95, -1022.08) * mm, v(3138.03, -1017) * mm, v(3205.44, -1014.5) * mm, v(3370.47, -1013.26) * mm]});
            skFitSpline(sketch, "E215", {"points": [v(3370.47, -1013.26) * mm, v(3571.54, -1011.75) * mm, v(3601.89, -1012.72) * mm, v(3608.66, -1020.88) * mm]});
            skFitSpline(sketch, "E216", {"points": [v(3608.66, -1020.88) * mm, v(3615.08, -1028.62) * mm, v(3605.62, -1073.57) * mm, v(3553.78, -1281.69) * mm]});
            skFitSpline(sketch, "E217", {"points": [v(3553.78, -1281.69) * mm, v(3472.06, -1609.74) * mm, v(3449.16, -1676.75) * mm, v(3400.78, -1729.6) * mm]});
            skFitSpline(sketch, "E218", {"points": [v(3400.78, -1729.6) * mm, v(3374.12, -1758.72) * mm, v(3372.21, -1765.12) * mm, v(3388.86, -1769.48) * mm]});
            skFitSpline(sketch, "E219", {"points": [v(3388.86, -1769.48) * mm, v(3395.3, -1771.16) * mm, v(3401.45, -1779) * mm, v(3402.58, -1786.95) * mm]});
            skLineSegment(sketch, "E220", {"start": v(344.08, -1779.5) * mm, "end": v(360.04, -1804.77) * mm});
            skLineSegment(sketch, "E221", {"start": v(360.04, -1804.77) * mm, "end": v(1053.27, -1802.82) * mm});
            skLineSegment(sketch, "E222", {"start": v(1053.27, -1802.82) * mm, "end": v(1746.5, -1800.88) * mm});
            skLineSegment(sketch, "E223", {"start": v(1746.5, -1800.88) * mm, "end": v(1794.1, -1787.18) * mm});
            skLineSegment(sketch, "E224", {"start": v(1794.1, -1787.18) * mm, "end": v(1794.1, -1787.18) * mm});
            skFitSpline(sketch, "E225", {"points": [v(4195.16, -1744.2) * mm, v(4194.1, -1712.74) * mm, v(4196.4, -1662) * mm, v(4200.29, -1631.41) * mm]});
            skFitSpline(sketch, "E226", {"points": [v(4200.29, -1631.41) * mm, v(4208.82, -1564.34) * mm, v(4539.96, -234.68) * mm, v(4565.7, -164.16) * mm]});
            skFitSpline(sketch, "E227", {"points": [v(4565.7, -164.16) * mm, v(4575.67, -136.84) * mm, v(4599, -86.1) * mm, v(4617.53, -51.38) * mm]});
            skFitSpline(sketch, "E228", {"points": [v(4617.53, -51.38) * mm, v(4651.2, 11.67) * mm, v(4651.22, 11.74) * mm, v(4638.88, 23.23) * mm]});
            skFitSpline(sketch, "E229", {"points": [v(4638.88, 23.23) * mm, v(4631.36, 30.24) * mm, v(4628.05, 38.66) * mm, v(4630.4, 44.8) * mm]});
            skFitSpline(sketch, "E230", {"points": [v(4630.4, 44.8) * mm, v(4634.16, 54.59) * mm, v(4625.22, 59.01) * mm, v(4611.62, 54.1) * mm]});
            skFitSpline(sketch, "E231", {"points": [v(4611.62, 54.1) * mm, v(4608.27, 52.9) * mm, v(4442.3, 49.96) * mm, v(4242.82, 47.59) * mm]});
            skFitSpline(sketch, "E232", {"points": [v(4242.82, 47.59) * mm, v(3858.92, 43.02) * mm, v(3840.83, 42.55) * mm, v(3839.87, 37.03) * mm]});
            skFitSpline(sketch, "E233", {"points": [v(3839.87, 37.03) * mm, v(3839.53, 35.1) * mm, v(3838.58, -4.88) * mm, v(3837.76, -51.82) * mm]});
            skFitSpline(sketch, "E234", {"points": [v(3837.76, -51.82) * mm, v(3836.08, -146.97) * mm, v(3837.08, -141.65) * mm, v(3767.7, -423.68) * mm]});
            skFitSpline(sketch, "E235", {"points": [v(3767.7, -423.68) * mm, v(3741.3, -530.97) * mm, v(3717.95, -629.78) * mm, v(3715.79, -643.26) * mm]});
            skFitSpline(sketch, "E236", {"points": [v(3715.79, -643.26) * mm, v(3713.63, -656.74) * mm, v(3709.57, -671.48) * mm, v(3706.76, -676.03) * mm]});
            skFitSpline(sketch, "E237", {"points": [v(3706.76, -676.03) * mm, v(3700.61, -685.97) * mm, v(3711.18, -685.64) * mm, v(3449.98, -684.04) * mm]});
            skFitSpline(sketch, "E238", {"points": [v(3449.98, -684.04) * mm, v(3284.06, -683.03) * mm, v(3236.9, -681) * mm, v(3228.02, -674.5) * mm]});
            skFitSpline(sketch, "E239", {"points": [v(3228.02, -674.5) * mm, v(3217.22, -666.6) * mm, v(3219, -657.12) * mm, v(3269.54, -452.54) * mm]});
            skFitSpline(sketch, "E240", {"points": [v(3269.54, -452.54) * mm, v(3337.01, -179.5) * mm, v(3357.82, -119.27) * mm, v(3423.33, -7.32) * mm]});
            skFitSpline(sketch, "E241", {"points": [v(3423.33, -7.32) * mm, v(3435, 12.62) * mm, v(3435, 12.87) * mm, v(3422.9, 21.92) * mm]});
            skFitSpline(sketch, "E242", {"points": [v(3422.9, 21.92) * mm, v(3416.2, 26.95) * mm, v(3411.57, 36.4) * mm, v(3412.62, 42.96) * mm]});
            skFitSpline(sketch, "E243", {"points": [v(3412.62, 42.96) * mm, v(3414.43, 54.23) * mm, v(3405.87, 58.96) * mm, v(3392.42, 54.1) * mm]});
            skFitSpline(sketch, "E244", {"points": [v(3392.42, 54.1) * mm, v(3389.07, 52.9) * mm, v(3223.1, 49.96) * mm, v(3023.62, 47.59) * mm]});
            skFitSpline(sketch, "E245", {"points": [v(3023.62, 47.59) * mm, v(2824.13, 45.21) * mm, v(2651.99, 42.66) * mm, v(2641.1, 41.9) * mm]});
            skLineSegment(sketch, "E246", {"start": v(3402.58, -1786.95) * mm, "end": v(3404.62, -1801.37) * mm});
            skLineSegment(sketch, "E247", {"start": v(3404.62, -1801.37) * mm, "end": v(3800.86, -1801.37) * mm});
            skLineSegment(sketch, "E248", {"start": v(3800.86, -1801.37) * mm, "end": v(4197.1, -1801.37) * mm});
            skLineSegment(sketch, "E249", {"start": v(4197.1, -1801.37) * mm, "end": v(4195.16, -1744.2) * mm});
            skFitSpline(sketch, "E250", {"points": [v(2621.28, -30.03) * mm, v(2621.28, -68.84) * mm, v(2616.95, -125.22) * mm, v(2611.68, -155.34) * mm]});
            skFitSpline(sketch, "E251", {"points": [v(2611.68, -155.34) * mm, v(2592.75, -263.6) * mm, v(2263.92, -1567.7) * mm, v(2239.7, -1630.59) * mm]});
            skFitSpline(sketch, "E252", {"points": [v(2239.7, -1630.59) * mm, v(2221.8, -1677.06) * mm, v(2209.14, -1699.32) * mm, v(2186.15, -1724.7) * mm]});
            skFitSpline(sketch, "E253", {"points": [v(2186.15, -1724.7) * mm, v(2156.3, -1757.67) * mm, v(2156.16, -1758.01) * mm, v(2169.22, -1766.68) * mm]});
            skFitSpline(sketch, "E254", {"points": [v(2169.22, -1766.68) * mm, v(2176.46, -1771.5) * mm, v(2182.39, -1780.12) * mm, v(2182.39, -1785.86) * mm]});
            skFitSpline(sketch, "E255", {"points": [v(2182.39, -1785.86) * mm, v(2182.39, -1791.6) * mm, v(2184.24, -1798.14) * mm, v(2186.5, -1800.4) * mm]});
            skFitSpline(sketch, "E256", {"points": [v(2186.5, -1800.4) * mm, v(2188.76, -1802.66) * mm, v(2367.75, -1803.8) * mm, v(2584.26, -1802.94) * mm]});
            skLineSegment(sketch, "E257", {"start": v(2641.1, 41.9) * mm, "end": v(2621.28, 40.53) * mm});
            skLineSegment(sketch, "E258", {"start": v(2621.28, 40.53) * mm, "end": v(2621.28, -30.03) * mm});
            skFitSpline(sketch, "E259", {"points": [v(6080.76, -1787.66) * mm, v(6190.95, -1756.93) * mm, v(6283.36, -1696.33) * mm, v(6352.66, -1609.35) * mm]});
            skFitSpline(sketch, "E260", {"points": [v(6352.66, -1609.35) * mm, v(6392.3, -1559.58) * mm, v(6451.48, -1445.7) * mm, v(6476.36, -1371.3) * mm]});
            skFitSpline(sketch, "E261", {"points": [v(6476.36, -1371.3) * mm, v(6497.04, -1309.45) * mm, v(6703.06, -483.85) * mm, v(6715.54, -412.83) * mm]});
            skFitSpline(sketch, "E262", {"points": [v(6715.54, -412.83) * mm, v(6728.56, -338.73) * mm, v(6728.54, -233.98) * mm, v(6715.48, -183.57) * mm]});
            skFitSpline(sketch, "E263", {"points": [v(6715.48, -183.57) * mm, v(6692.71, -95.59) * mm, v(6639.43, -25.28) * mm, v(6569.47, 9.08) * mm]});
            skFitSpline(sketch, "E264", {"points": [v(6569.47, 9.08) * mm, v(6488.15, 49.02) * mm, v(6475.94, 49.64) * mm, v(5809.83, 47.35) * mm]});
            skLineSegment(sketch, "E265", {"start": v(2584.26, -1802.94) * mm, "end": v(2977.9, -1801.37) * mm});
            skLineSegment(sketch, "E266", {"start": v(2977.9, -1801.37) * mm, "end": v(2978.48, -1719.08) * mm});
            skLineSegment(sketch, "E267", {"start": v(2978.48, -1719.08) * mm, "end": v(2978.48, -1719.08) * mm});
            skFitSpline(sketch, "E268", {"points": [v(5160.25, 28.75) * mm, v(4978.44, -20.69) * mm, v(4839.15, -136.44) * mm, v(4764.6, -300.03) * mm]});
            skFitSpline(sketch, "E269", {"points": [v(4764.6, -300.03) * mm, v(4753.28, -324.87) * mm, v(4733.98, -376.26) * mm, v(4721.7, -414.23) * mm]});
            skFitSpline(sketch, "E270", {"points": [v(4721.7, -414.23) * mm, v(4693.66, -500.98) * mm, v(4501.63, -1270.18) * mm, v(4489.55, -1344.17) * mm]});
            skFitSpline(sketch, "E271", {"points": [v(4489.55, -1344.17) * mm, v(4477.97, -1415.1) * mm, v(4477.99, -1529.1) * mm, v(4489.61, -1572.73) * mm]});
            skFitSpline(sketch, "E272", {"points": [v(4489.61, -1572.73) * mm, v(4512.94, -1660.4) * mm, v(4569.01, -1733) * mm, v(4639.22, -1766.43) * mm]});
            skFitSpline(sketch, "E273", {"points": [v(4639.22, -1766.43) * mm, v(4719.4, -1804.6) * mm, v(4700.49, -1803.7) * mm, v(5398, -1802.43) * mm]});
            skLineSegment(sketch, "E274", {"start": v(5809.83, 47.35) * mm, "end": v(5221.2, 45.33) * mm});
            skLineSegment(sketch, "E275", {"start": v(5221.2, 45.33) * mm, "end": v(5160.25, 28.75) * mm});
            skFitSpline(sketch, "E276", {"points": [v(5239.51, -1467.86) * mm, v(5209.75, -1457.43) * mm, v(5199.89, -1445.24) * mm, v(5199.89, -1418.88) * mm]});
            skFitSpline(sketch, "E277", {"points": [v(5199.89, -1418.88) * mm, v(5199.89, -1391.57) * mm, v(5451.91, -379) * mm, v(5465.02, -353.65) * mm]});
            skFitSpline(sketch, "E278", {"points": [v(5465.02, -353.65) * mm, v(5477.62, -329.3) * mm, v(5513.27, -300.28) * mm, v(5539.57, -292.98) * mm]});
            skFitSpline(sketch, "E279", {"points": [v(5539.57, -292.98) * mm, v(5571.11, -284.22) * mm, v(5953.78, -284.33) * mm, v(5978.95, -293.1) * mm]});
            skFitSpline(sketch, "E280", {"points": [v(5978.95, -293.1) * mm, v(6020.46, -307.57) * mm, v(6023.67, -288.64) * mm, v(5885.92, -841.86) * mm]});
            skFitSpline(sketch, "E281", {"points": [v(5885.92, -841.86) * mm, v(5817.13, -1118.13) * mm, v(5756.34, -1361.54) * mm, v(5750.83, -1382.77) * mm]});
            skFitSpline(sketch, "E282", {"points": [v(5750.83, -1382.77) * mm, v(5739.52, -1426.31) * mm, v(5718.88, -1454.68) * mm, v(5689.57, -1466.92) * mm]});
            skFitSpline(sketch, "E283", {"points": [v(5689.57, -1466.92) * mm, v(5664.62, -1477.35) * mm, v(5268.93, -1478.18) * mm, v(5239.51, -1467.86) * mm]});
            skLineSegment(sketch, "E284", {"start": v(5398, -1802.43) * mm, "end": v(6031.99, -1801.26) * mm});
            skLineSegment(sketch, "E285", {"start": v(6031.99, -1801.26) * mm, "end": v(6080.76, -1787.66) * mm});
            skLineSegment(sketch, "E286", {"start": v(6080.76, -1787.66) * mm, "end": v(6080.76, -1787.66) * mm});
            skLineSegment(sketch, "E287", {"start": v(6080.76, -1787.66) * mm, "end": v(5398, -1802.43) * mm});
            skFitSpline(sketch, "E288", {"points": [v(7355.97, -1797.79) * mm, v(7360.32, -1793.44) * mm, v(7361.5, -1769.65) * mm, v(7359.4, -1728.57) * mm]});
            skFitSpline(sketch, "E289", {"points": [v(7359.4, -1728.57) * mm, v(7357.57, -1692.71) * mm, v(7359.4, -1644.12) * mm, v(7363.68, -1614.8) * mm]});
            skFitSpline(sketch, "E290", {"points": [v(7363.68, -1614.8) * mm, v(7372.86, -1551.86) * mm, v(7465.58, -1177.16) * mm, v(7474.7, -1166.19) * mm]});
            skFitSpline(sketch, "E291", {"points": [v(7474.7, -1166.19) * mm, v(7479.98, -1159.82) * mm, v(7556.42, -1158.24) * mm, v(7860.9, -1158.24) * mm]});
            skFitSpline(sketch, "E292", {"points": [v(7860.9, -1158.24) * mm, v(8078.73, -1158.24) * mm, v(8266.69, -1155.56) * mm, v(8301.95, -1151.94) * mm]});
            skFitSpline(sketch, "E293", {"points": [v(8301.95, -1151.94) * mm, v(8533.27, -1128.2) * mm, v(8667.9, -1021.03) * mm, v(8746.56, -798) * mm]});
            skFitSpline(sketch, "E294", {"points": [v(8746.56, -798) * mm, v(8766.84, -740.5) * mm, v(8853.05, -398.55) * mm, v(8863.22, -335.28) * mm]});
            skFitSpline(sketch, "E295", {"points": [v(8863.22, -335.28) * mm, v(8877.71, -245.11) * mm, v(8868.31, -160.93) * mm, v(8836.84, -98.96) * mm]});
            skFitSpline(sketch, "E296", {"points": [v(8836.84, -98.96) * mm, v(8800.1, -26.62) * mm, v(8742.17, 14.72) * mm, v(8649.6, 34.68) * mm]});
            skFitSpline(sketch, "E297", {"points": [v(8649.6, 34.68) * mm, v(8601.64, 45.02) * mm, v(8549.22, 45.69) * mm, v(7818.12, 45.29) * mm]});
            skFitSpline(sketch, "E298", {"points": [v(7818.12, 45.29) * mm, v(7388.96, 45.05) * mm, v(7025.84, 44.12) * mm, v(7011.2, 43.22) * mm]});
            skLineSegment(sketch, "E299", {"start": v(5239.51, -1467.86) * mm, "end": v(5239.51, -1467.86) * mm});
            skFitSpline(sketch, "E300", {"points": [v(6988.55, 13.17) * mm, v(6999.03, -61.2) * mm, v(6999.33, -104.03) * mm, v(6989.8, -160) * mm]});
            skFitSpline(sketch, "E301", {"points": [v(6989.8, -160) * mm, v(6979.28, -221.69) * mm, v(6667.35, -1478.75) * mm, v(6640.74, -1566.68) * mm]});
            skFitSpline(sketch, "E302", {"points": [v(6640.74, -1566.68) * mm, v(6618.8, -1639.14) * mm, v(6594.74, -1689.66) * mm, v(6565.8, -1723.99) * mm]});
            skFitSpline(sketch, "E303", {"points": [v(6565.8, -1723.99) * mm, v(6539, -1755.78) * mm, v(6536, -1764.61) * mm, v(6550.15, -1770.05) * mm]});
            skFitSpline(sketch, "E304", {"points": [v(6550.15, -1770.05) * mm, v(6555.18, -1771.98) * mm, v(6559.3, -1778.67) * mm, v(6559.3, -1784.92) * mm]});
            skFitSpline(sketch, "E305", {"points": [v(6559.3, -1784.92) * mm, v(6559.3, -1791.18) * mm, v(6561.12, -1798.12) * mm, v(6563.36, -1800.36) * mm]});
            skFitSpline(sketch, "E306", {"points": [v(6563.36, -1800.36) * mm, v(6570.66, -1807.66) * mm, v(7348.62, -1805.14) * mm, v(7355.97, -1797.79) * mm]});
            skLineSegment(sketch, "E307", {"start": v(7011.2, 43.22) * mm, "end": v(6984.55, 41.59) * mm});
            skLineSegment(sketch, "E308", {"start": v(6984.55, 41.59) * mm, "end": v(6988.55, 13.17) * mm});
            skFitSpline(sketch, "E309", {"points": [v(7728.87, -824.5) * mm, v(7612.45, -823.2) * mm, v(7570.93, -820.8) * mm, v(7566.19, -815.09) * mm]});
            skFitSpline(sketch, "E310", {"points": [v(7566.19, -815.09) * mm, v(7558.9, -806.31) * mm, v(7679.98, -311.53) * mm, v(7693.36, -295.41) * mm]});
            skFitSpline(sketch, "E311", {"points": [v(7693.36, -295.41) * mm, v(7704.84, -281.58) * mm, v(8117.04, -284.71) * mm, v(8126.51, -298.7) * mm]});
            skFitSpline(sketch, "E312", {"points": [v(8126.51, -298.7) * mm, v(8129.92, -303.74) * mm, v(8131.45, -325.68) * mm, v(8129.92, -347.48) * mm]});
            skFitSpline(sketch, "E313", {"points": [v(8129.92, -347.48) * mm, v(8126.8, -392.11) * mm, v(8046.51, -723.05) * mm, v(8029.04, -763.3) * mm]});
            skFitSpline(sketch, "E314", {"points": [v(8029.04, -763.3) * mm, v(8008.15, -811.47) * mm, v(7976.74, -829.97) * mm, v(7919.83, -827.64) * mm]});
            skFitSpline(sketch, "E315", {"points": [v(7919.83, -827.64) * mm, v(7900.77, -826.87) * mm, v(7814.84, -825.45) * mm, v(7728.87, -824.5) * mm]});
            skLineSegment(sketch, "E316", {"start": v(7355.97, -1797.79) * mm, "end": v(7355.97, -1797.79) * mm});
            skFitSpline(sketch, "E317", {"points": [v(-454.59, 247.32) * mm, v(-442.96, 258.94) * mm, v(-442.93, 266.94) * mm, v(-454.28, 313.94) * mm]});
            skFitSpline(sketch, "E318", {"points": [v(-454.28, 313.94) * mm, v(-465.54, 360.59) * mm, v(-465.79, 467.44) * mm, v(-454.77, 525.24) * mm]});
            skFitSpline(sketch, "E319", {"points": [v(-454.77, 525.24) * mm, v(-449.49, 552.95) * mm, v(-447.75, 583.89) * mm, v(-450.2, 606.55) * mm]});
            skFitSpline(sketch, "E320", {"points": [v(-478.54, 645.15) * mm, v(-491.95, 646.27) * mm, v(-659.28, 642.81) * mm, v(-850.4, 637.47) * mm]});
            skFitSpline(sketch, "E321", {"points": [v(-850.4, 637.47) * mm, v(-1041.5, 632.12) * mm, v(-1348.74, 623.65) * mm, v(-1533.15, 618.64) * mm]});
            skFitSpline(sketch, "E322", {"points": [v(-1533.15, 618.64) * mm, v(-1717.55, 613.63) * mm, v(-2018.62, 605.43) * mm, v(-2202.18, 600.42) * mm]});
            skFitSpline(sketch, "E323", {"points": [v(-2202.18, 600.42) * mm, v(-2385.75, 595.4) * mm, v(-2686.13, 587.21) * mm, v(-2869.7, 582.2) * mm]});
            skFitSpline(sketch, "E324", {"points": [v(-2869.7, 582.2) * mm, v(-3053.26, 577.2) * mm, v(-3354.33, 569) * mm, v(-3538.73, 563.96) * mm]});
            skFitSpline(sketch, "E325", {"points": [v(-3538.73, 563.96) * mm, v(-3723.13, 558.93) * mm, v(-4027.63, 550.65) * mm, v(-4215.39, 545.56) * mm]});
            skFitSpline(sketch, "E326", {"points": [v(-4215.39, 545.56) * mm, v(-4403.14, 540.47) * mm, v(-4704.9, 532.24) * mm, v(-4885.95, 527.26) * mm]});
            skFitSpline(sketch, "E327", {"points": [v(-4885.95, 527.26) * mm, v(-5067, 522.28) * mm, v(-5368.75, 514.05) * mm, v(-5556.5, 508.96) * mm]});
            skFitSpline(sketch, "E328", {"points": [v(-5556.5, 508.96) * mm, v(-5744.26, 503.88) * mm, v(-6044.64, 495.72) * mm, v(-6224.02, 490.83) * mm]});
            skFitSpline(sketch, "E329", {"points": [v(-6224.02, 490.83) * mm, v(-6403.4, 485.94) * mm, v(-6712, 477.7) * mm, v(-6909.82, 472.52) * mm]});
            skFitSpline(sketch, "E330", {"points": [v(-6909.82, 472.52) * mm, v(-7107.63, 467.33) * mm, v(-7292.8, 461.29) * mm, v(-7321.3, 459.09) * mm]});
            skFitSpline(sketch, "E331", {"points": [v(-7321.3, 459.09) * mm, v(-7369.51, 455.36) * mm, v(-7371.2, 454.78) * mm, v(-7345.68, 450.85) * mm]});
            skFitSpline(sketch, "E332", {"points": [v(-7345.68, 450.85) * mm, v(-7330.6, 448.52) * mm, v(-7262.01, 444.73) * mm, v(-7193.28, 442.42) * mm]});
            skFitSpline(sketch, "E333", {"points": [v(-7193.28, 442.42) * mm, v(-7031.9, 437) * mm, v(-6827.04, 422.45) * mm, v(-6807.53, 415.03) * mm]});
            skFitSpline(sketch, "E334", {"points": [v(-6807.53, 415.03) * mm, v(-6790.13, 408.42) * mm, v(-6581.45, 399.18) * mm, v(-6248.4, 390.29) * mm]});
            skFitSpline(sketch, "E335", {"points": [v(-6248.4, 390.29) * mm, v(-6122.67, 386.93) * mm, v(-5969.05, 382.7) * mm, v(-5907.03, 380.9) * mm]});
            skFitSpline(sketch, "E336", {"points": [v(-5907.03, 380.9) * mm, v(-5845, 379.08) * mm, v(-5639.26, 373.57) * mm, v(-5449.83, 368.64) * mm]});
            skFitSpline(sketch, "E337", {"points": [v(-5449.83, 368.64) * mm, v(-5260.4, 363.7) * mm, v(-5003.9, 356.91) * mm, v(-4879.85, 353.54) * mm]});
            skFitSpline(sketch, "E338", {"points": [v(-4879.85, 353.54) * mm, v(-4755.8, 350.17) * mm, v(-4449.93, 341.93) * mm, v(-4200.15, 335.23) * mm]});
            skFitSpline(sketch, "E339", {"points": [v(-4200.15, 335.23) * mm, v(-3950.36, 328.53) * mm, v(-3440.13, 314.82) * mm, v(-3066.3, 304.77) * mm]});
            skFitSpline(sketch, "E340", {"points": [v(-3066.3, 304.77) * mm, v(-2692.45, 294.71) * mm, v(-2077.98, 278.23) * mm, v(-1700.79, 268.15) * mm]});
            skFitSpline(sketch, "E341", {"points": [v(-1700.79, 268.15) * mm, v(-1323.6, 258.06) * mm, v(-940.92, 247.51) * mm, v(-850.4, 244.72) * mm]});
            skFitSpline(sketch, "E342", {"points": [v(-850.4, 244.72) * mm, v(-559.45, 235.72) * mm, v(-465.57, 236.34) * mm, v(-454.59, 247.32) * mm]});
            skLineSegment(sketch, "E343", {"start": v(-450.2, 606.55) * mm, "end": v(-454.15, 643.12) * mm});
            skLineSegment(sketch, "E344", {"start": v(-454.15, 643.12) * mm, "end": v(-478.54, 645.15) * mm});
            skFitSpline(sketch, "E345", {"points": [v(1176.53, 249.99) * mm, v(1292.2, 253.2) * mm, v(1593.95, 261.37) * mm, v(1847.09, 268.11) * mm]});
            skFitSpline(sketch, "E346", {"points": [v(1847.09, 268.11) * mm, v(2100.22, 274.86) * mm, v(2456.84, 284.5) * mm, v(2639.57, 289.54) * mm]});
            skFitSpline(sketch, "E347", {"points": [v(2639.57, 289.54) * mm, v(2822.3, 294.58) * mm, v(3177.54, 304.22) * mm, v(3429, 310.97) * mm]});
            skFitSpline(sketch, "E348", {"points": [v(3429, 310.97) * mm, v(4217.76, 332.15) * mm, v(4549.54, 341.1) * mm, v(4779.26, 347.4) * mm]});
            skFitSpline(sketch, "E349", {"points": [v(4779.26, 347.4) * mm, v(4901.64, 350.76) * mm, v(5159.5, 357.55) * mm, v(5352.29, 362.5) * mm]});
            skFitSpline(sketch, "E350", {"points": [v(5352.29, 362.5) * mm, v(5545.07, 367.43) * mm, v(5748.07, 373) * mm, v(5803.4, 374.88) * mm]});
            skFitSpline(sketch, "E351", {"points": [v(5803.4, 374.88) * mm, v(5858.71, 376.75) * mm, v(6064.45, 382.34) * mm, v(6260.6, 387.31) * mm]});
            skFitSpline(sketch, "E352", {"points": [v(6260.6, 387.31) * mm, v(6711.66, 398.73) * mm, v(6885.67, 406.43) * mm, v(6943.34, 417.53) * mm]});
            skFitSpline(sketch, "E353", {"points": [v(6943.34, 417.53) * mm, v(6998.52, 428.15) * mm, v(7122.57, 437.16) * mm, v(7289.97, 442.7) * mm]});
            skFitSpline(sketch, "E354", {"points": [v(7289.97, 442.7) * mm, v(7358.23, 444.97) * mm, v(7422.7, 448.72) * mm, v(7433.22, 451.04) * mm]});
            skFitSpline(sketch, "E355", {"points": [v(7433.22, 451.04) * mm, v(7465.03, 458.05) * mm, v(7376.1, 462.37) * mm, v(6992.11, 472.45) * mm]});
            skFitSpline(sketch, "E356", {"points": [v(6992.11, 472.45) * mm, v(6795.97, 477.6) * mm, v(6488.73, 485.85) * mm, v(6309.36, 490.79) * mm]});
            skFitSpline(sketch, "E357", {"points": [v(6309.36, 490.79) * mm, v(6129.99, 495.73) * mm, v(5831.66, 503.9) * mm, v(5646.42, 508.96) * mm]});
            skFitSpline(sketch, "E358", {"points": [v(5646.42, 508.96) * mm, v(5461.18, 514.02) * mm, v(5159.43, 522.27) * mm, v(4975.86, 527.3) * mm]});
            skFitSpline(sketch, "E359", {"points": [v(4975.86, 527.3) * mm, v(4583.85, 538.05) * mm, v(4105.14, 551.12) * mm, v(3633.22, 563.96) * mm]});
            skFitSpline(sketch, "E360", {"points": [v(3633.22, 563.96) * mm, v(3447.14, 569.03) * mm, v(3148.13, 577.21) * mm, v(2968.75, 582.15) * mm]});
            skFitSpline(sketch, "E361", {"points": [v(2968.75, 582.15) * mm, v(2789.38, 587.1) * mm, v(2487.63, 595.34) * mm, v(2298.2, 600.49) * mm]});
            skFitSpline(sketch, "E362", {"points": [v(2298.2, 600.49) * mm, v(1971.12, 609.36) * mm, v(1817.48, 613.6) * mm, v(940.32, 637.9) * mm]});
            skFitSpline(sketch, "E363", {"points": [v(940.32, 637.9) * mm, v(734.97, 643.58) * mm, v(565.18, 646.45) * mm, v(563, 644.28) * mm]});
            skFitSpline(sketch, "E364", {"points": [v(563, 644.28) * mm, v(560.83, 642.1) * mm, v(563.82, 617.64) * mm, v(569.66, 589.9) * mm]});
            skFitSpline(sketch, "E365", {"points": [v(569.66, 589.9) * mm, v(585.5, 514.64) * mm, v(588.68, 397.68) * mm, v(576.43, 341.37) * mm]});
            skFitSpline(sketch, "E366", {"points": [v(576.43, 341.37) * mm, v(570.96, 316.23) * mm, v(564.87, 288.1) * mm, v(562.9, 278.89) * mm]});
            skFitSpline(sketch, "E367", {"points": [v(562.9, 278.89) * mm, v(559.92, 264.96) * mm, v(561.39, 262.12) * mm, v(571.59, 262.12) * mm]});
            skFitSpline(sketch, "E368", {"points": [v(571.59, 262.12) * mm, v(578.34, 262.12) * mm, v(590.34, 256.47) * mm, v(598.26, 249.55) * mm]});
            skFitSpline(sketch, "E369", {"points": [v(598.26, 249.55) * mm, v(612.3, 237.28) * mm, v(616.96, 237.07) * mm, v(789.43, 240.55) * mm]});
            skFitSpline(sketch, "E370", {"points": [v(789.43, 240.55) * mm, v(886.66, 242.52) * mm, v(1060.86, 246.76) * mm, v(1176.53, 249.99) * mm]});
            skLineSegment(sketch, "E371", {"start": v(-454.59, 247.32) * mm, "end": v(-454.59, 247.32) * mm});
            skFitSpline(sketch, "E372", {"points": [v(-369.26, 734.23) * mm, v(-328.2, 787.83) * mm, v(-270.48, 843.17) * mm, v(-219.53, 877.77) * mm]});
            skFitSpline(sketch, "E373", {"points": [v(-219.53, 877.77) * mm, v(-192.86, 895.88) * mm, v(-182.88, 906.41) * mm, v(-182.88, 916.45) * mm]});
            skFitSpline(sketch, "E374", {"points": [v(-182.88, 916.45) * mm, v(-182.88, 924.04) * mm, v(-179.59, 933.54) * mm, v(-175.56, 937.56) * mm]});
            skFitSpline(sketch, "E375", {"points": [v(-175.56, 937.56) * mm, v(-170.96, 942.17) * mm, v(-170.4, 946.97) * mm, v(-174.04, 950.52) * mm]});
            skFitSpline(sketch, "E376", {"points": [v(-174.04, 950.52) * mm, v(-180.13, 956.46) * mm, v(-675.48, 1248.55) * mm, v(-707.8, 1265.26) * mm]});
            skFitSpline(sketch, "E377", {"points": [v(-707.8, 1265.26) * mm, v(-718.12, 1270.6) * mm, v(-728.04, 1273.47) * mm, v(-729.86, 1271.66) * mm]});
            skFitSpline(sketch, "E378", {"points": [v(-729.86, 1271.66) * mm, v(-735.75, 1265.76) * mm, v(-719.74, 1232.33) * mm, v(-579.93, 958.6) * mm]});
            skFitSpline(sketch, "E379", {"points": [v(-579.93, 958.6) * mm, v(-442.68, 689.87) * mm, v(-442.08, 688.84) * mm, v(-423.09, 688.84) * mm]});
            skFitSpline(sketch, "E380", {"points": [v(-423.09, 688.84) * mm, v(-406.56, 688.84) * mm, v(-399.41, 694.86) * mm, v(-369.26, 734.23) * mm]});
            skFitSpline(sketch, "E381", {"points": [v(599.52, 720.85) * mm, v(610.65, 738.45) * mm, v(672.65, 846.85) * mm, v(737.3, 961.74) * mm]});
            skFitSpline(sketch, "E382", {"points": [v(737.3, 961.74) * mm, v(829.8, 1126.15) * mm, v(854.17, 1174.04) * mm, v(851.76, 1186.66) * mm]});
            skFitSpline(sketch, "E383", {"points": [v(851.76, 1186.66) * mm, v(850.07, 1195.48) * mm, v(852.81, 1214.79) * mm, v(857.85, 1229.56) * mm]});
            skFitSpline(sketch, "E384", {"points": [v(857.85, 1229.56) * mm, v(862.88, 1244.34) * mm, v(865.54, 1257.9) * mm, v(863.75, 1259.68) * mm]});
            skFitSpline(sketch, "E385", {"points": [v(863.75, 1259.68) * mm, v(860.18, 1263.25) * mm, v(313.16, 972.42) * mm, v(299.23, 959.55) * mm]});
            skFitSpline(sketch, "E386", {"points": [v(299.23, 959.55) * mm, v(291.92, 952.8) * mm, v(295.34, 947.33) * mm, v(321.65, 923.67) * mm]});
            skFitSpline(sketch, "E387", {"points": [v(321.65, 923.67) * mm, v(338.72, 908.32) * mm, v(368.66, 883.9) * mm, v(388.18, 869.4) * mm]});
            skFitSpline(sketch, "E388", {"points": [v(388.18, 869.4) * mm, v(436.06, 833.84) * mm, v(492.5, 773.26) * mm, v(520.9, 726.94) * mm]});
            skFitSpline(sketch, "E389", {"points": [v(520.9, 726.94) * mm, v(540.82, 694.48) * mm, v(546.87, 688.84) * mm, v(561.77, 688.84) * mm]});
            skFitSpline(sketch, "E390", {"points": [v(561.77, 688.84) * mm, v(576.25, 688.84) * mm, v(582.77, 694.38) * mm, v(599.52, 720.85) * mm]});
            skFitSpline(sketch, "E391", {"points": [v(79.25, 959.9) * mm, v(127.86, 959.78) * mm, v(182.35, 958.42) * mm, v(200.32, 956.86) * mm]});
            skFitSpline(sketch, "E392", {"points": [v(200.32, 956.86) * mm, v(225.82, 954.64) * mm, v(234.4, 956.17) * mm, v(239.36, 963.8) * mm]});
            skFitSpline(sketch, "E393", {"points": [v(239.36, 963.8) * mm, v(248.82, 978.38) * mm, v(83.4, 1566.28) * mm, v(62.97, 1590.65) * mm]});
            skFitSpline(sketch, "E394", {"points": [v(62.97, 1590.65) * mm, v(56.11, 1598.83) * mm, v(41.15, 1554.38) * mm, v(-42.44, 1277.54) * mm]});
            skFitSpline(sketch, "E395", {"points": [v(-42.44, 1277.54) * mm, v(-132.5, 979.29) * mm, v(-137.44, 957.6) * mm, v(-113.15, 966.91) * mm]});
            skFitSpline(sketch, "E396", {"points": [v(-113.15, 966.91) * mm, v(-109.4, 968.35) * mm, v(-100.92, 965.27) * mm, v(-94.31, 960.08) * mm]});
            skFitSpline(sketch, "E397", {"points": [v(-94.31, 960.08) * mm, v(-84.75, 952.55) * mm, v(-74.82, 951.6) * mm, v(-45.72, 955.37) * mm]});
            skFitSpline(sketch, "E398", {"points": [v(-45.72, 955.37) * mm, v(-25.6, 957.98) * mm, v(30.63, 960.02) * mm, v(79.25, 959.9) * mm]});
            skLineSegment(sketch, "E399", {"start": v(-4431.8, -272) * mm, "end": v(-4457.34, -358.18) * mm});
            skLineSegment(sketch, "E400", {"start": v(-4457.34, -358.18) * mm, "end": v(-4320.6, -328.43) * mm});
            skSolve(sketch);
        }
        {
            var Q0;
            Q0 = qSketchRegion(id + "F0", true);
            extrude(context, id + "F1", {"entities" : qUnion([Q0]), "depth" : 25.4 * mm});
        }
    });
